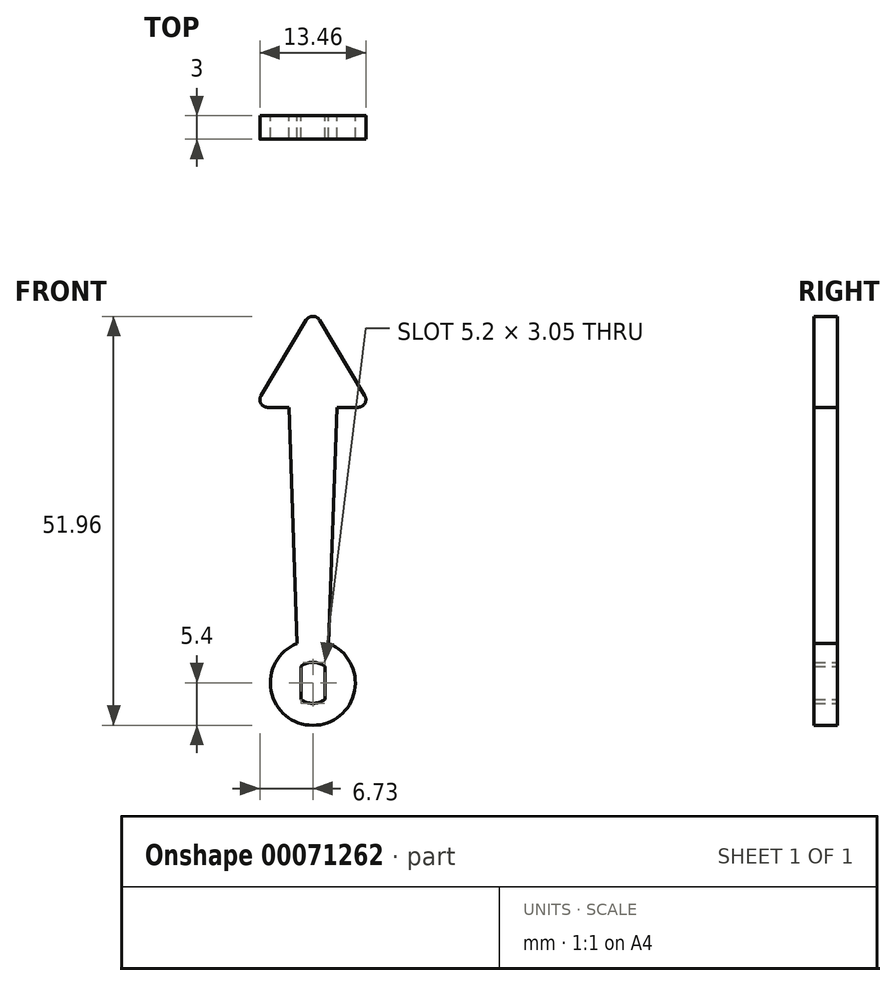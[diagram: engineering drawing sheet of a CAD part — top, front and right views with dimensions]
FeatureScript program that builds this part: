
annotation { "Feature Type Name" : "Feature", "Feature Type Description" : "" }
export const myFeature = defineFeature(function(context is Context, id is Id, definition is map)
    precondition{}
    {
        {
            var Q0;
            Q0=qCreatedBy(makeId("Front.planeOp"),FACE);
            var sketch = newSketch(context, id + "F0", { "sketchPlane" : qUnion([Q0])});
            skCircle(sketch, "E0", {"center": v(0, 0) * mm, "radius": 2.6 * mm});
            skCircle(sketch, "E1", {"center": v(0, 0) * mm, "radius": 5.4 * mm});
            skLineSegment(sketch, "E2", {"start": v(-1.53, -2.1) * mm, "end": v(-1.53, 2.1) * mm});
            skLineSegment(sketch, "E3", {"start": v(1.52, 2.1) * mm, "end": v(1.52, -2.1) * mm});
            skSolve(sketch);
        }
        {
            var Q0;
            Q0=makeQuery(id+"F0.imprint","IMPRINT",FACE,{"disambiguationData":[TD([[makeQuery(id+"F0.imprint","IMPRINT",EDGE,{"derivedFrom":sQuery(id+"F0.wireOp",EDGE,"E1")}),1.0]])]});
            var Q1;
            {var subQ0=sQuery(id+"F0.wireOp",EDGE,"E2");Q1=makeQuery(id+"F0.imprint","IMPRINT",FACE,{"disambiguationData":[TD([[makeQuery(id+"F0.imprint","IMPRINT",EDGE,{"derivedFrom":subQ0}),1.0]])]});}
            var Q2;
            {var subQ0=sQuery(id+"F0.wireOp",EDGE,"E3");Q2=makeQuery(id+"F0.imprint","IMPRINT",FACE,{"disambiguationData":[TD([[makeQuery(id+"F0.imprint","IMPRINT",EDGE,{"derivedFrom":subQ0}),1.0]])]});}
            extrude(context, id + "F1", {"entities" : qUnion([Q0, Q1, Q2]), "endBound" : BoundingType.SYMMETRIC, "depth" : 3 * mm});
        }
        {
            var Q0;
            Q0=qCreatedBy(makeId("Front.planeOp"),FACE);
            var sketch = newSketch(context, id + "F2", { "sketchPlane" : qUnion([Q0])});
            skLineSegment(sketch, "E4", {"start": v(0, 0) * mm, "end": v(0, -1469.51) * mm});
            skLineSegment(sketch, "E5", {"start": v(0, 0) * mm, "end": v(0, 35) * mm, "construction": true});
            skLineSegment(sketch, "E6", {"start": v(0, 35) * mm, "end": v(3.05, 35) * mm});
            skLineSegment(sketch, "E7", {"start": v(3.05, 35) * mm, "end": v(2, 5.02) * mm});
            skLineSegment(sketch, "E8", {"start": v(2, 5.02) * mm, "end": v(0, 5.02) * mm});
            skLineSegment(sketch, "E9.MirrorCS", {"start": v(0, 35) * mm, "end": v(-3.05, 35) * mm});
            skLineSegment(sketch, "E10.MirrorCS", {"start": v(-3.05, 35) * mm, "end": v(-2, 5.02) * mm});
            skLineSegment(sketch, "E11.MirrorCS", {"start": v(-2, 5.02) * mm, "end": v(0, 5.02) * mm});
            skSolve(sketch);
        }
        {
            var Q0;
            Q0=makeQuery(id+"F2.imprint","IMPRINT",FACE,{"disambiguationData":[TD([[makeQuery(id+"F2.imprint","IMPRINT",EDGE,{"derivedFrom":sQuery(id+"F2.wireOp",EDGE,"E6")}),-1.0]])]});
            var Q1;
            Q1=makeQuery(id+"F1.opExtrude","CAP_FACE",FACE,{"disambiguationData":[OSD([sQuery(id+"F0.wireOp",EDGE,"E0"),sQuery(id+"F0.wireOp",EDGE,"E1"),sQuery(id+"F0.wireOp",EDGE,"E2"),sQuery(id+"F0.wireOp",EDGE,"E3")])],"isStart":false});
            extrude(context, id + "F3", {"entities" : qUnion([Q0]), "operationType" : NewBodyOperationType.ADD, "endBound" : BoundingType.SYMMETRIC, "endBoundEntityFace" : qUnion([Q1]), "depth" : 3 * mm});
        }
        {
            var Q0;
            Q0=qCreatedBy(makeId("Front.planeOp"),FACE);
            var sketch = newSketch(context, id + "F4", { "sketchPlane" : qUnion([Q0])});
            skLineSegment(sketch, "E12", {"start": v(0, 35) * mm, "end": v(0, 47.5) * mm, "construction": true});
            skLineSegment(sketch, "E13", {"start": v(-7.5, 35) * mm, "end": v(7.5, 35) * mm});
            skLineSegment(sketch, "E14", {"start": v(0, 47.5) * mm, "end": v(-7.5, 35) * mm});
            skLineSegment(sketch, "E15", {"start": v(0, 47.5) * mm, "end": v(7.5, 35) * mm});
            skSolve(sketch);
        }
        {
            var Q0;
            Q0=makeQuery(id+"F4.imprint","IMPRINT",FACE,{"disambiguationData":[TD([[makeQuery(id+"F4.imprint","IMPRINT",EDGE,{"derivedFrom":sQuery(id+"F4.wireOp",EDGE,"E13")}),1.0]])]});
            extrude(context, id + "F5", {"entities" : qUnion([Q0]), "operationType" : NewBodyOperationType.ADD, "endBound" : BoundingType.SYMMETRIC, "depth" : 3 * mm});
        }
        {
            var Q0;
            Q0=makeQuery(id+"F5.opExtrude","SWEPT_EDGE",EDGE,{"disambiguationData":[OSD([sQuery(id+"F4.wireOp",EDGE,"E13"),sQuery(id+"F4.wireOp",EDGE,"E14")])]});
            var Q1;
            Q1=makeQuery(id+"F5.opExtrude","SWEPT_EDGE",EDGE,{"disambiguationData":[OSD([sQuery(id+"F4.wireOp",EDGE,"E14"),sQuery(id+"F4.wireOp",EDGE,"E15")])]});
            var Q2;
            Q2=makeQuery(id+"F5.opExtrude","SWEPT_EDGE",EDGE,{"disambiguationData":[OSD([sQuery(id+"F4.wireOp",EDGE,"E13"),sQuery(id+"F4.wireOp",EDGE,"E15")])]});
            fillet(context, id + "F6", {"entities" : qUnion([Q0, Q1, Q2]), "radius" : 1 * mm, "tangentPropagation" : true, "allowEdgeOverflow" : false});
        }
    });
